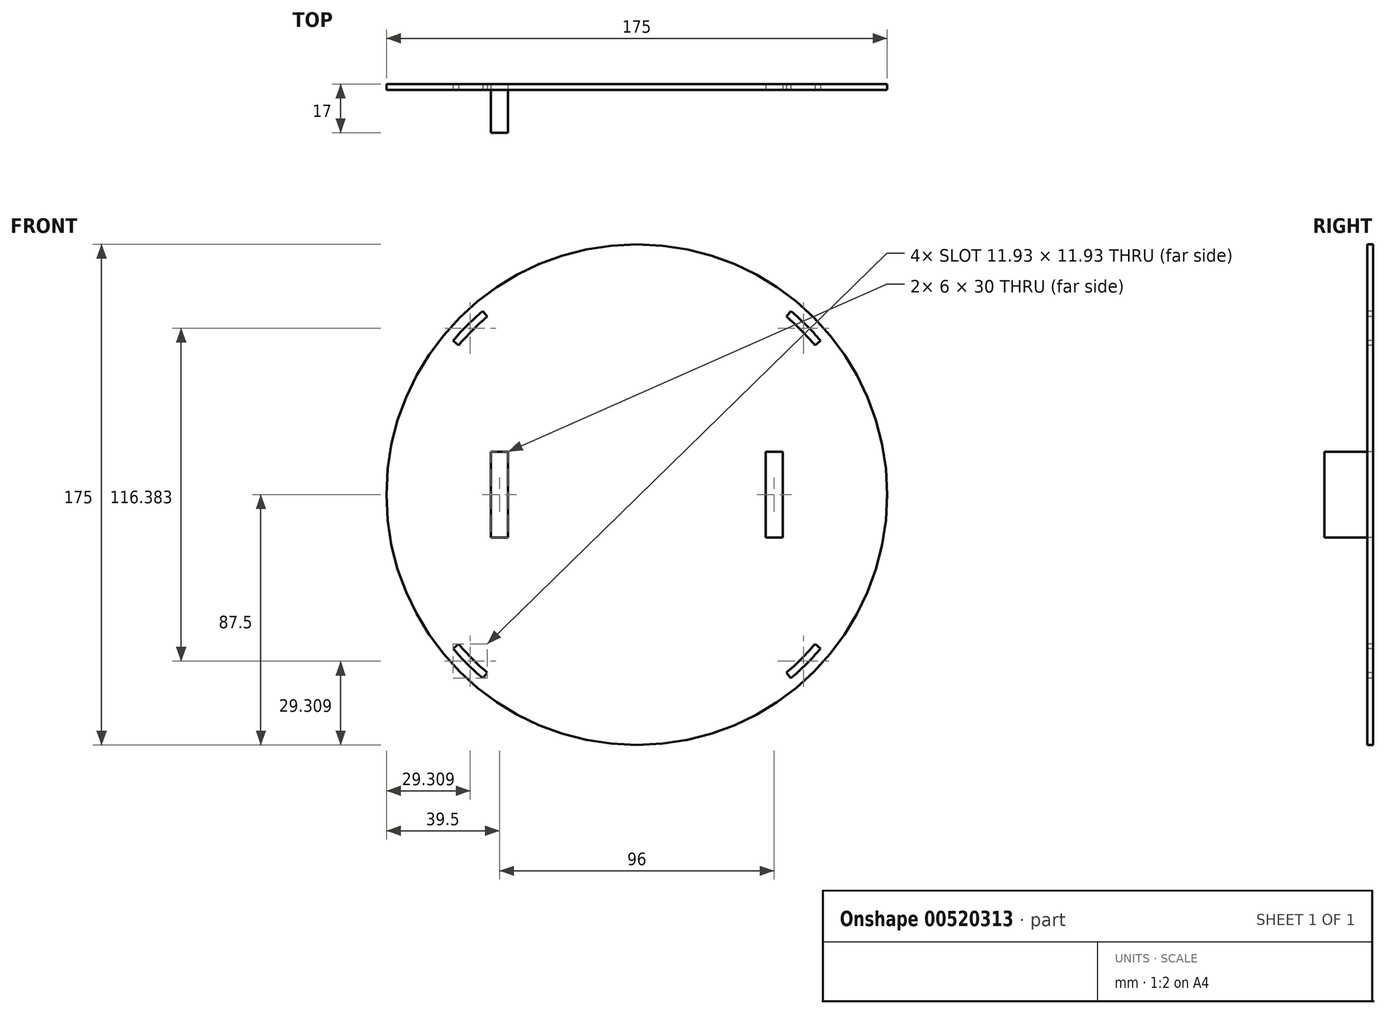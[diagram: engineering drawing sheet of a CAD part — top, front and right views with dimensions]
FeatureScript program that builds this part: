
annotation { "Feature Type Name" : "Feature", "Feature Type Description" : "" }
export const myFeature = defineFeature(function(context is Context, id is Id, definition is map)
    precondition{}
    {
        {
            var Q0;
            Q0=qCreatedBy(makeId("Front.planeOp"),FACE);
            var sketch = newSketch(context, id + "F0", { "sketchPlane" : qUnion([Q0])});
            skCircle(sketch, "E0", {"center": v(0, 0) * mm, "radius": 87.5 * mm});
            skLineSegment(sketch, "E1", {"start": v(52.23, -62.24) * mm, "end": v(53.83, -64.16) * mm});
            skLineSegment(sketch, "E2", {"start": v(64.16, -53.83) * mm, "end": v(62.24, -52.23) * mm});
            skArc(sketch, "E3", {"start": v(52.23, -62.24) * mm, "mid": v(57.45, -57.45) * mm, "end": v(62.24, -52.23) * mm});
            skArc(sketch, "E4", {"start": v(53.83, -64.16) * mm, "mid": v(59.22, -59.22) * mm, "end": v(64.16, -53.83) * mm});
            skLineSegment(sketch, "E5", {"start": v(-64.16, -53.83) * mm, "end": v(-62.24, -52.23) * mm});
            skLineSegment(sketch, "E6", {"start": v(-53.83, -64.16) * mm, "end": v(-52.23, -62.24) * mm});
            skArc(sketch, "E7", {"start": v(-62.24, -52.23) * mm, "mid": v(-57.45, -57.45) * mm, "end": v(-52.23, -62.24) * mm});
            skArc(sketch, "E8", {"start": v(-64.16, -53.83) * mm, "mid": v(-59.22, -59.22) * mm, "end": v(-53.83, -64.16) * mm});
            skLineSegment(sketch, "E9", {"start": v(-53.83, 64.16) * mm, "end": v(-52.23, 62.24) * mm});
            skLineSegment(sketch, "E10", {"start": v(-64.16, 53.83) * mm, "end": v(-62.24, 52.23) * mm});
            skArc(sketch, "E11", {"start": v(-62.24, 52.23) * mm, "mid": v(-57.45, 57.45) * mm, "end": v(-52.23, 62.24) * mm});
            skArc(sketch, "E12", {"start": v(-64.16, 53.83) * mm, "mid": v(-59.22, 59.22) * mm, "end": v(-53.83, 64.16) * mm});
            skLineSegment(sketch, "E13", {"start": v(64.16, 53.83) * mm, "end": v(62.24, 52.23) * mm});
            skLineSegment(sketch, "E14", {"start": v(53.83, 64.16) * mm, "end": v(52.23, 62.24) * mm});
            skArc(sketch, "E15", {"start": v(52.23, 62.24) * mm, "mid": v(57.45, 57.45) * mm, "end": v(62.24, 52.23) * mm});
            skArc(sketch, "E16", {"start": v(64.16, 53.83) * mm, "mid": v(59.22, 59.22) * mm, "end": v(53.83, 64.16) * mm});
            skLineSegment(sketch, "E17", {"start": v(-45, 0) * mm, "end": v(-45, -15) * mm});
            skLineSegment(sketch, "E18", {"start": v(-45, -15) * mm, "end": v(-51, -15) * mm});
            skLineSegment(sketch, "E19", {"start": v(-51, -15) * mm, "end": v(-51, 15) * mm});
            skLineSegment(sketch, "E20", {"start": v(-51, 15) * mm, "end": v(-45, 15) * mm});
            skLineSegment(sketch, "E21", {"start": v(-45, 15) * mm, "end": v(-45, 0) * mm});
            skLineSegment(sketch, "E22", {"start": v(51, -15) * mm, "end": v(51, 15) * mm});
            skLineSegment(sketch, "E23", {"start": v(51, 15) * mm, "end": v(45, 15) * mm});
            skLineSegment(sketch, "E24", {"start": v(45, 15) * mm, "end": v(45, 0) * mm});
            skLineSegment(sketch, "E25", {"start": v(45, 0) * mm, "end": v(45, -15) * mm});
            skLineSegment(sketch, "E26", {"start": v(45, -15) * mm, "end": v(51, -15) * mm});
            skSolve(sketch);
        }
        {
            var Q0;
            Q0 = qSketchRegion(id + "F0", true);
            extrude(context, id + "F1", {"entities" : qUnion([Q0]), "oppositeDirection" : true, "depth" : 2 * mm, "offsetDistance" : 25 * mm});
        }
        {
            var Q0;
            Q0=makeQuery(id+"F0.imprint","IMPRINT",FACE,{"disambiguationData":[TD([[makeQuery(id+"F0.imprint","IMPRINT",EDGE,{"derivedFrom":sQuery(id+"F0.wireOp",EDGE,"E17")}),-1.0]])]});
            var Q1;
            Q1=makeQuery(id+"F0.imprint","IMPRINT",FACE,{"disambiguationData":[TD([[makeQuery(id+"F0.imprint","IMPRINT",EDGE,{"derivedFrom":sQuery(id+"F0.wireOp",EDGE,"80efd8e4-c225-42d3-a6ad-3276b2480e27")}),1.0]])]});
            extrude(context, id + "F2", {"entities" : qUnion([Q0, Q1]), "depth" : 15 * mm, "offsetDistance" : 25 * mm});
        }
    });
